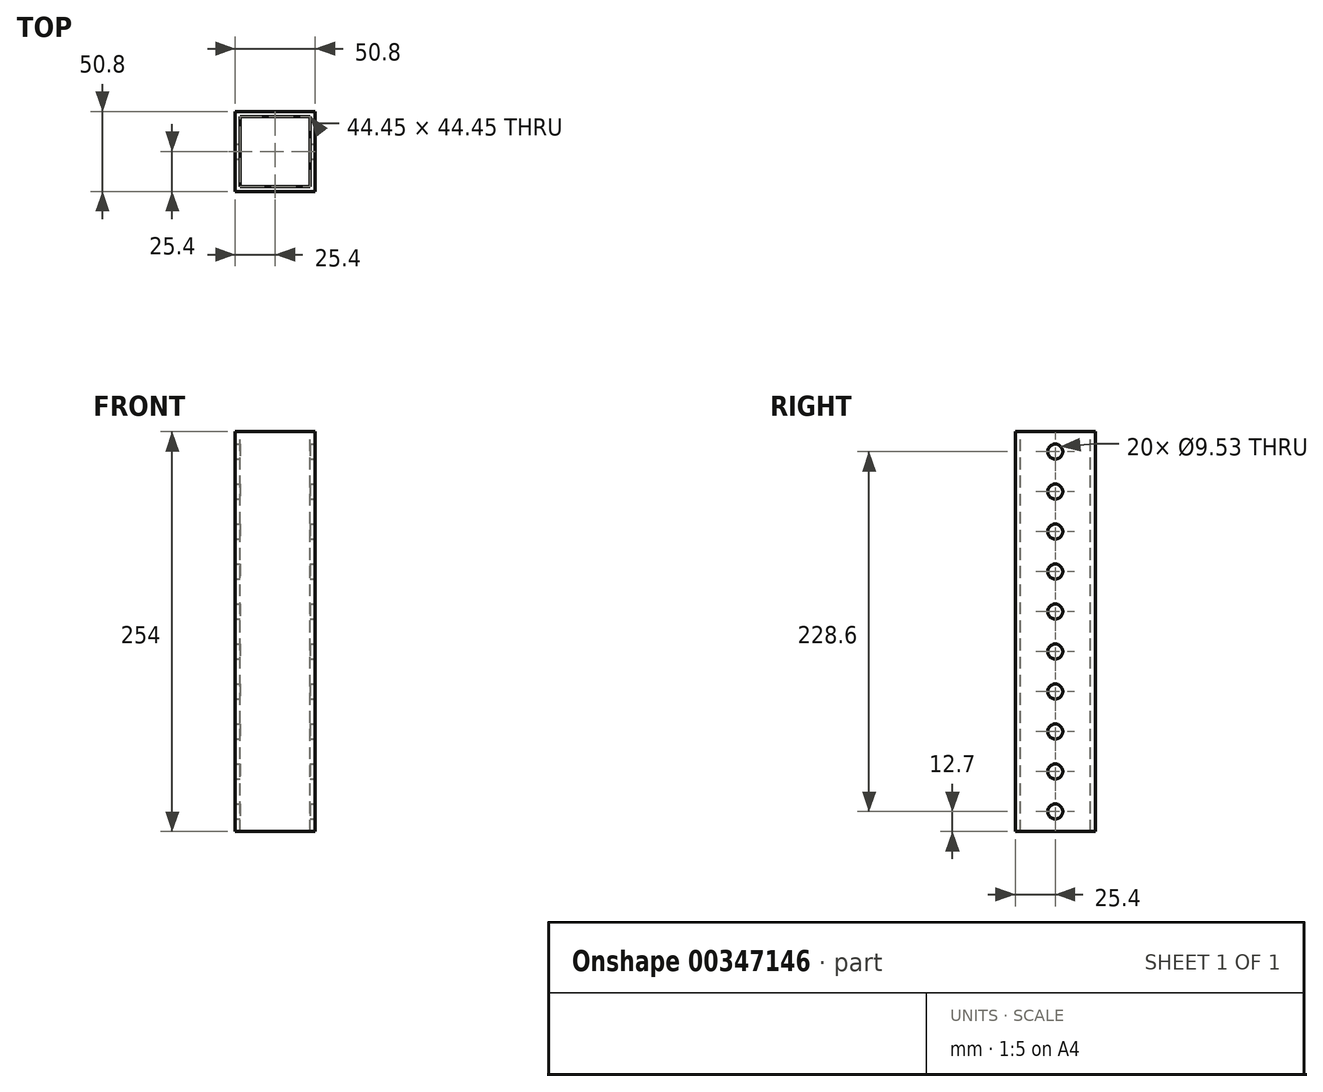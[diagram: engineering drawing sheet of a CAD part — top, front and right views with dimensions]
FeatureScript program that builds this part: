
annotation { "Feature Type Name" : "Feature", "Feature Type Description" : "" }
export const myFeature = defineFeature(function(context is Context, id is Id, definition is map)
    precondition{}
    {
        {
            var Q0;
            Q0=qCreatedBy(makeId("Top.planeOp"),FACE);
            var sketch = newSketch(context, id + "F0", { "sketchPlane" : qUnion([Q0])});
            skLineSegment(sketch, "E0.bottom", {"start": v(0, 0) * mm, "end": v(50.8, 0) * mm});
            skLineSegment(sketch, "E0.top", {"start": v(0, 50.8) * mm, "end": v(50.8, 50.8) * mm});
            skLineSegment(sketch, "E0.left", {"start": v(0, 0) * mm, "end": v(0, 50.8) * mm});
            skLineSegment(sketch, "E0.right", {"start": v(50.8, 0) * mm, "end": v(50.8, 50.8) * mm});
            skSolve(sketch);
        }
        {
            var Q0;
            Q0=makeQuery(id+"F0.imprint","IMPRINT",FACE,{"disambiguationData":[TD([[makeQuery(id+"F0.imprint","IMPRINT",EDGE,{"derivedFrom":sQuery(id+"F0.wireOp",EDGE,"E0.bottom")}),1.0]])]});
            extrude(context, id + "F1", {"entities" : qUnion([Q0]), "depth" : 254 * mm});
        }
        {
            var Q0;
            Q0=makeQuery(id+"F1.opExtrude","CAP_FACE",FACE,{"disambiguationData":[OSD([sQuery(id+"F0.wireOp",EDGE,"E0.bottom"),sQuery(id+"F0.wireOp",EDGE,"E0.top"),sQuery(id+"F0.wireOp",EDGE,"E0.left"),sQuery(id+"F0.wireOp",EDGE,"E0.right")])],"isStart":false});
            var sketch = newSketch(context, id + "F2", { "sketchPlane" : qUnion([Q0])});
            skLineSegment(sketch, "E1.bottom", {"start": v(47.62, 47.62) * mm, "end": v(3.17, 47.62) * mm});
            skLineSegment(sketch, "E1.top", {"start": v(47.62, 3.18) * mm, "end": v(3.18, 3.18) * mm});
            skLineSegment(sketch, "E1.left", {"start": v(47.62, 47.62) * mm, "end": v(47.62, 3.17) * mm});
            skLineSegment(sketch, "E1.right", {"start": v(3.18, 47.62) * mm, "end": v(3.18, 3.18) * mm});
            skPoint(sketch, "E1.middle", {"position": v(25.4, 25.4) * mm});
            skPoint(sketch, "E1.middle.positionSnap0", {"position": v(25.4, 50.8) * mm});
            skPoint(sketch, "E1.middle.positionSnap1", {"position": v(50.8, 25.4) * mm});
            skPoint(sketch, "E1.centerSnap0", {"position": v(25.4, 50.8) * mm});
            skPoint(sketch, "E1.centerSnap1", {"position": v(50.8, 25.4) * mm});
            skSolve(sketch);
        }
        {
            var Q0;
            Q0=makeQuery(id+"F2.imprint","IMPRINT",FACE,{"disambiguationData":[TD([[makeQuery(id+"F2.imprint","IMPRINT",EDGE,{"derivedFrom":sQuery(id+"F2.wireOp",EDGE,"E1.bottom")}),1.0]])]});
            extrude(context, id + "F3", {"entities" : qUnion([Q0]), "operationType" : NewBodyOperationType.REMOVE, "endBound" : BoundingType.THROUGH_ALL, "oppositeDirection" : true, "depth" : 25.4 * mm});
        }
        {
            var Q0;
            Q0=makeQuery(id+"F1.opExtrude","SWEPT_FACE",FACE,{"disambiguationData":[OSD([sQuery(id+"F0.wireOp",EDGE,"E0.right")])]});
            var sketch = newSketch(context, id + "F4", { "sketchPlane" : qUnion([Q0])});
            skCircle(sketch, "E2", {"center": v(25.4, 12.7) * mm, "radius": 4.76 * mm});
            skLineSegment(sketch, "E3", {"start": v(0, 12.7) * mm, "end": v(50.8, 12.7) * mm, "construction": true});
            skCircle(sketch, "E4.0.1.0", {"center": v(25.4, 38.1) * mm, "radius": 4.76 * mm});
            skCircle(sketch, "E4.0.2.0", {"center": v(25.4, 63.5) * mm, "radius": 4.76 * mm});
            skCircle(sketch, "E4.0.3.0", {"center": v(25.4, 88.9) * mm, "radius": 4.76 * mm});
            skCircle(sketch, "E4.0.4.0", {"center": v(25.4, 114.3) * mm, "radius": 4.76 * mm});
            skCircle(sketch, "E4.0.5.0", {"center": v(25.4, 139.7) * mm, "radius": 4.76 * mm});
            skCircle(sketch, "E4.0.6.0", {"center": v(25.4, 165.1) * mm, "radius": 4.76 * mm});
            skCircle(sketch, "E4.0.7.0", {"center": v(25.4, 190.5) * mm, "radius": 4.76 * mm});
            skCircle(sketch, "E4.0.8.0", {"center": v(25.4, 215.9) * mm, "radius": 4.76 * mm});
            skCircle(sketch, "E4.0.9.0", {"center": v(25.4, 241.3) * mm, "radius": 4.76 * mm});
            skLineSegment(sketch, "E4.direction1", {"start": v(25.4, 12.7) * mm, "end": v(38.1, 12.7) * mm, "construction": true});
            skLineSegment(sketch, "E4.direction2", {"start": v(25.4, 12.7) * mm, "end": v(25.4, 38.1) * mm, "construction": true});
            skSolve(sketch);
        }
        {
            var Q0;
            Q0 = qSketchRegion(id + "F4", true);
            extrude(context, id + "F5", {"entities" : qUnion([Q0]), "operationType" : NewBodyOperationType.REMOVE, "endBound" : BoundingType.THROUGH_ALL, "oppositeDirection" : true, "depth" : 25.4 * mm});
        }
    });
